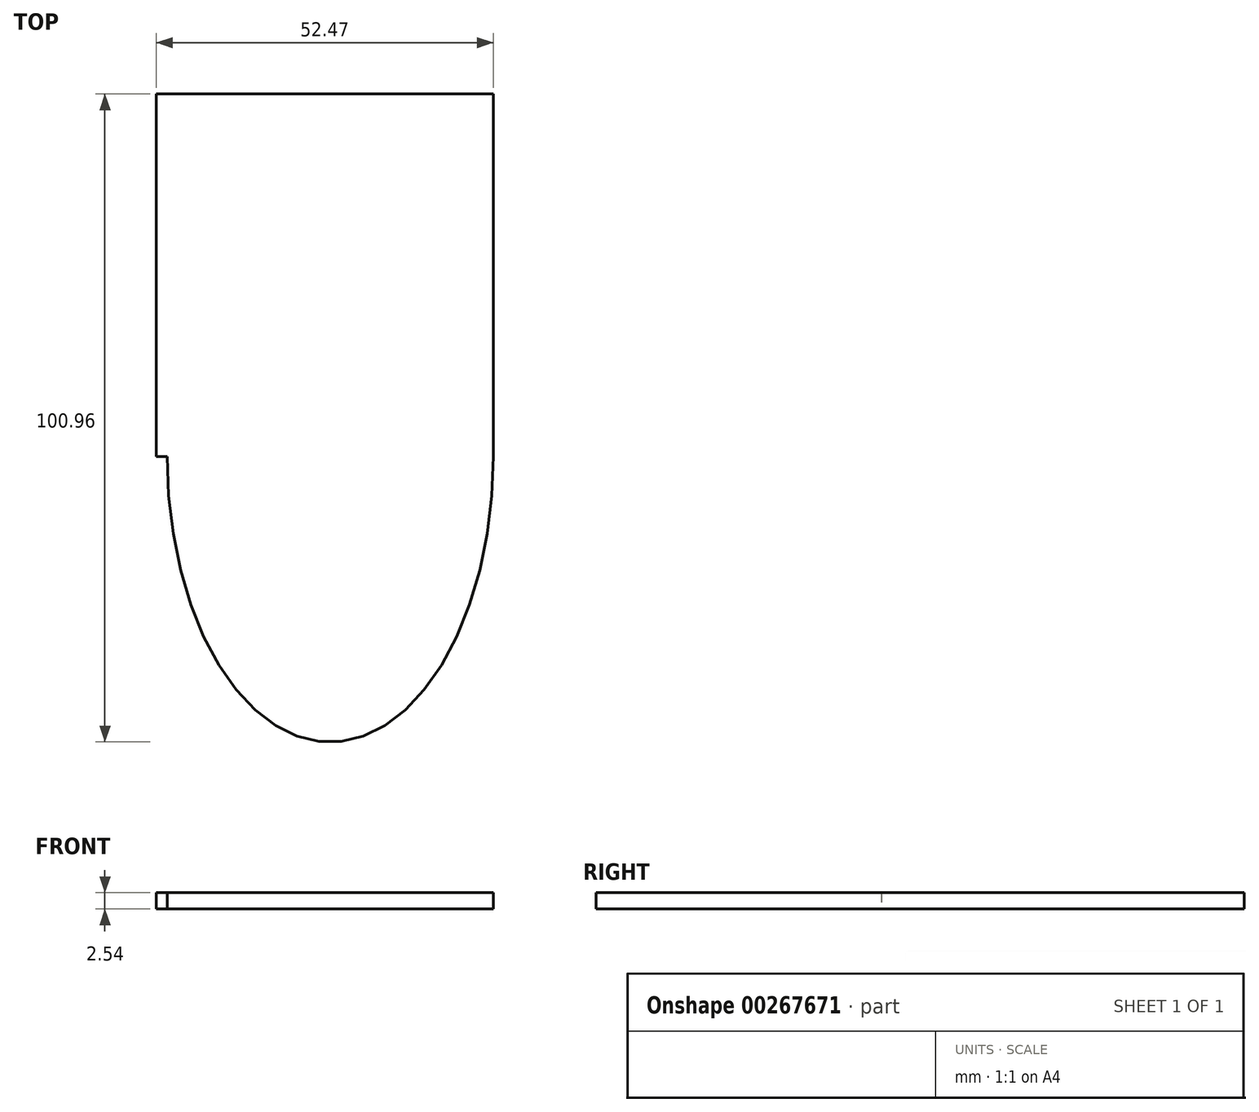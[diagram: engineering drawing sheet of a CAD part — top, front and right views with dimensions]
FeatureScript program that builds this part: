
annotation { "Feature Type Name" : "Feature", "Feature Type Description" : "" }
export const myFeature = defineFeature(function(context is Context, id is Id, definition is map)
    precondition{}
    {
        {
            var Q0;
            Q0=qCreatedBy(makeId("Top.planeOp"),FACE);
            var sketch = newSketch(context, id + "F0", { "sketchPlane" : qUnion([Q0])});
            skEllipse(sketch, "E0", {"center": v(0, 0) * mm, "majorRadius": 44.45 * mm, "minorRadius": 25.4 * mm, "majorAxis": v(0, 1)});
            skPoint(sketch, "E1", {"position": v(0, 44.45) * mm});
            skLineSegment(sketch, "E2.bottom", {"start": v(25.4, 0) * mm, "end": v(-27.07, 0) * mm});
            skLineSegment(sketch, "E2.top", {"start": v(25.4, 56.5) * mm, "end": v(-27.07, 56.5) * mm});
            skLineSegment(sketch, "E2.left", {"start": v(25.4, 0) * mm, "end": v(25.4, 56.5) * mm});
            skLineSegment(sketch, "E2.right", {"start": v(-27.07, 0) * mm, "end": v(-27.07, 56.5) * mm});
            skSolve(sketch);
        }
        {
            var Q0;
            Q0 = qSketchRegion(id + "F0", true);
            extrude(context, id + "F1", {"entities" : qUnion([Q0]), "depth" : 2.54 * mm});
        }
    });
